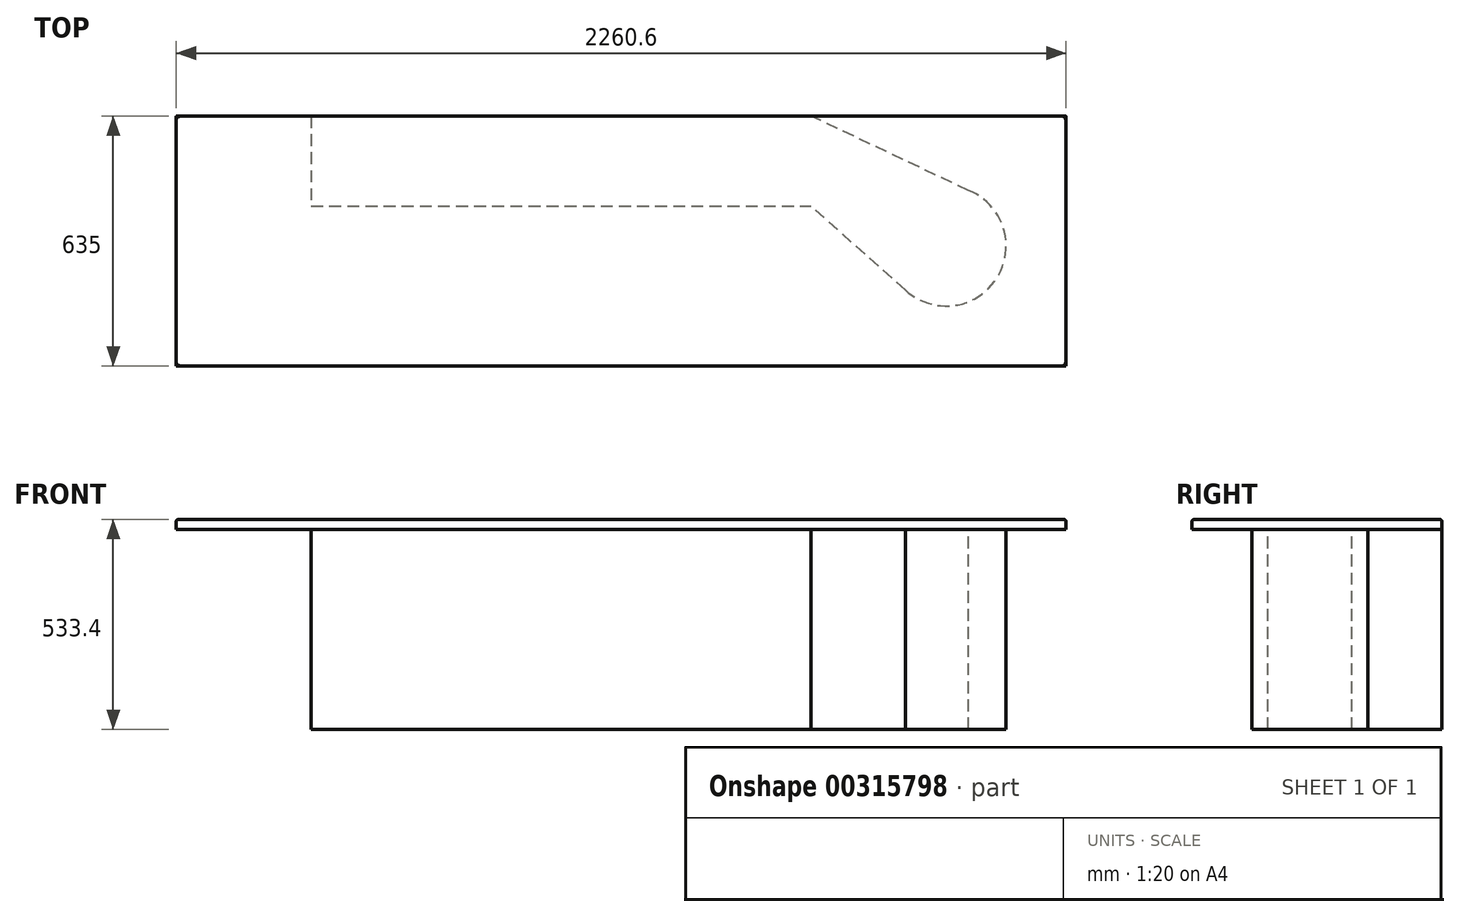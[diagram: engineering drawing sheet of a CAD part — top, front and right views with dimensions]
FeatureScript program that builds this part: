
annotation { "Feature Type Name" : "Feature", "Feature Type Description" : "" }
export const myFeature = defineFeature(function(context is Context, id is Id, definition is map)
    precondition{}
    {
        {
            var Q0;
            Q0=qCreatedBy(makeId("Top.planeOp"),FACE);
            var sketch = newSketch(context, id + "F0", { "sketchPlane" : qUnion([Q0])});
            skLineSegment(sketch, "E0.bottom", {"start": v(0, 0) * mm, "end": v(2260.6, 0) * mm});
            skLineSegment(sketch, "E0.top", {"start": v(0, 635) * mm, "end": v(2260.6, 635) * mm});
            skLineSegment(sketch, "E0.left", {"start": v(0, 0) * mm, "end": v(0, 635) * mm});
            skLineSegment(sketch, "E0.right", {"start": v(2260.6, 0) * mm, "end": v(2260.6, 635) * mm});
            skSolve(sketch);
        }
        {
            var Q0;
            Q0=makeQuery(id+"F0.imprint","IMPRINT",FACE,{"disambiguationData":[TD([[makeQuery(id+"F0.imprint","IMPRINT",EDGE,{"derivedFrom":sQuery(id+"F0.wireOp",EDGE,"E0.bottom")}),1.0]])]});
            extrude(context, id + "F1", {"entities" : qUnion([Q0]), "depth" : 25.4 * mm});
        }
        {
            var Q0;
            Q0=makeQuery(id+"F1.opExtrude","CAP_FACE",FACE,{"disambiguationData":[OSD([sQuery(id+"F0.wireOp",EDGE,"E0.bottom"),sQuery(id+"F0.wireOp",EDGE,"E0.top"),sQuery(id+"F0.wireOp",EDGE,"E0.left"),sQuery(id+"F0.wireOp",EDGE,"E0.right")])],"isStart":false});
            fillet(context, id + "F2", {"entities" : qUnion([Q0]), "radius" : 5.08 * mm, "tangentPropagation" : true, "allowEdgeOverflow" : false});
        }
        {
            var Q0;
            Q0=makeQuery(id+"F1.opExtrude","CAP_FACE",FACE,{"disambiguationData":[OSD([sQuery(id+"F0.wireOp",EDGE,"E0.bottom"),sQuery(id+"F0.wireOp",EDGE,"E0.top"),sQuery(id+"F0.wireOp",EDGE,"E0.left"),sQuery(id+"F0.wireOp",EDGE,"E0.right")])],"isStart":true});
            var sketch = newSketch(context, id + "F3", { "sketchPlane" : qUnion([Q0])});
            skLineSegment(sketch, "E1.bottom", {"start": v(342.9, -635) * mm, "end": v(1612.9, -635) * mm});
            skLineSegment(sketch, "E1.top", {"start": v(342.9, -406.4) * mm, "end": v(1612.9, -406.4) * mm});
            skLineSegment(sketch, "E1.left", {"start": v(342.9, -635) * mm, "end": v(342.9, -406.4) * mm});
            skLineSegment(sketch, "E1.right", {"start": v(1612.9, -635) * mm, "end": v(1612.9, -406.4) * mm});
            skCircle(sketch, "E2", {"center": v(1955.8, -304.8) * mm, "radius": 152.4 * mm});
            skLineSegment(sketch, "E3", {"start": v(2028.94, -438.5) * mm, "end": v(1612.9, -635) * mm});
            skLineSegment(sketch, "E4", {"start": v(1856.64, -189.07) * mm, "end": v(1612.9, -406.4) * mm});
            skSolve(sketch);
        }
        {
            var Q0;
            Q0 = qSketchRegion(id + "F3", true);
            extrude(context, id + "F4", {"entities" : qUnion([Q0]), "operationType" : NewBodyOperationType.ADD, "depth" : 508 * mm});
        }
    });
